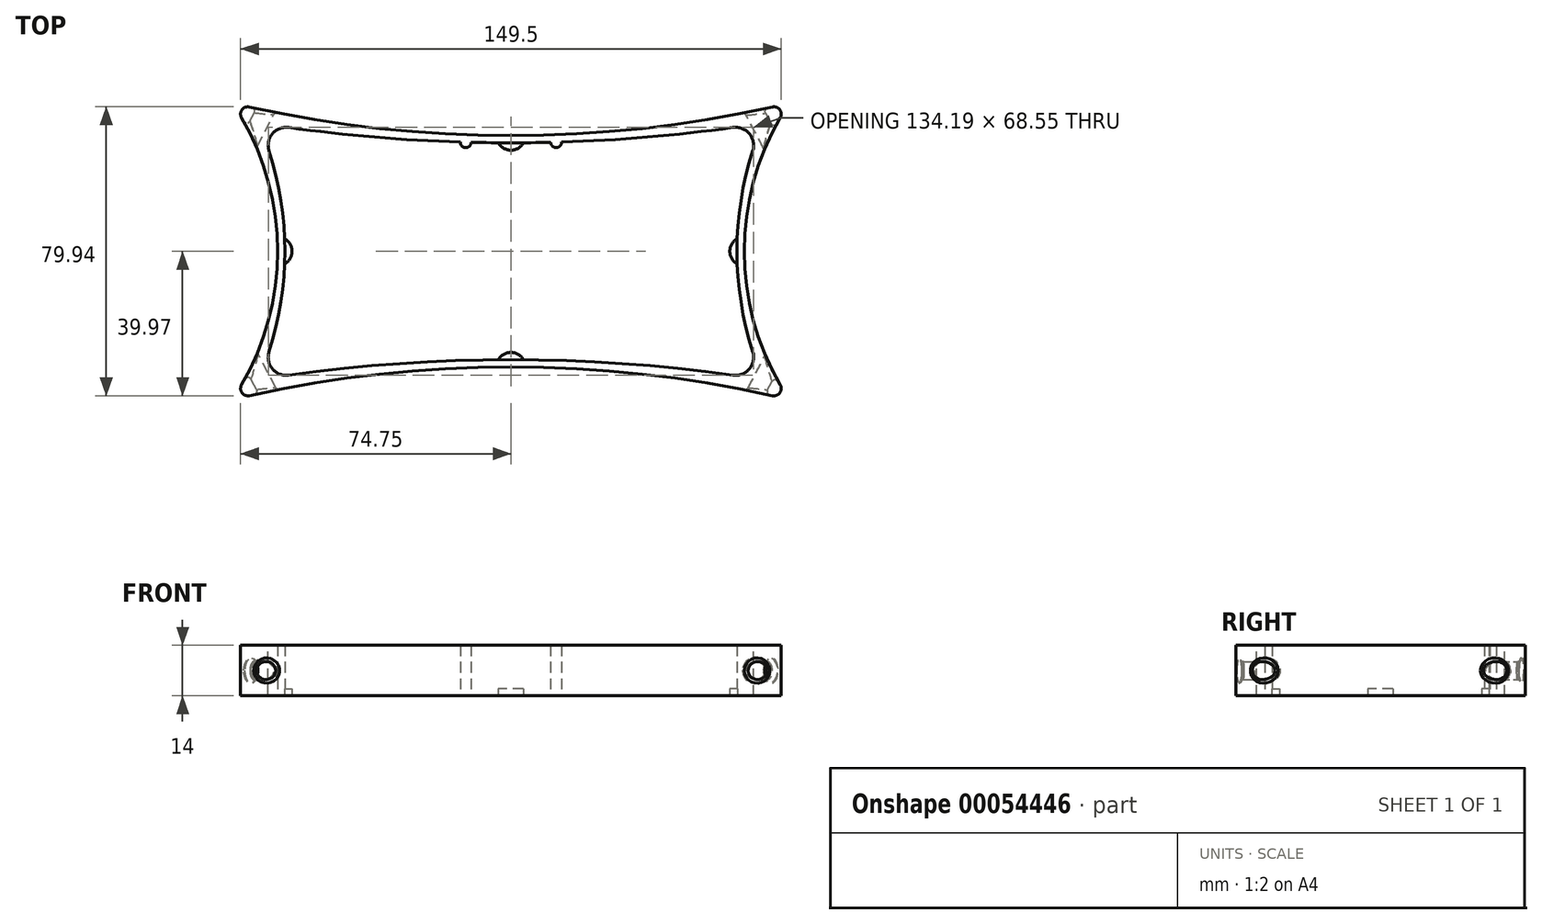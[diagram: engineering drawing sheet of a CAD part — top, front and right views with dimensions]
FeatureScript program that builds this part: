
annotation { "Feature Type Name" : "Feature", "Feature Type Description" : "" }
export const myFeature = defineFeature(function(context is Context, id is Id, definition is map)
    precondition{}
    {
        {
            var Q0;
            Q0=qCreatedBy(makeId("Top.planeOp"),FACE);
            var sketch = newSketch(context, id + "F0", { "sketchPlane" : qUnion([Q0])});
            skLineSegment(sketch, "E0.rect.bottom", {"start": v(77, -41) * mm, "end": v(-77, -41) * mm, "construction": true});
            skLineSegment(sketch, "E0.rect.top", {"start": v(77, 41) * mm, "end": v(-77, 41) * mm, "construction": true});
            skLineSegment(sketch, "E0.rect.left", {"start": v(77, -41) * mm, "end": v(77, 41) * mm, "construction": true});
            skLineSegment(sketch, "E0.rect.right", {"start": v(-77, -41) * mm, "end": v(-77, 41) * mm, "construction": true});
            skPoint(sketch, "E0.rect.middle", {"position": v(0, 0) * mm});
            skPoint(sketch, "E1.endSnap0", {"position": v(-77, 0) * mm});
            skPoint(sketch, "E2.endSnap0", {"position": v(0, 41) * mm});
            skLineSegment(sketch, "E3.rect.bottom", {"start": v(-62.5, 30) * mm, "end": v(62.5, 30) * mm, "construction": true});
            skLineSegment(sketch, "E3.rect.top", {"start": v(-62.5, -30) * mm, "end": v(62.5, -30) * mm, "construction": true});
            skLineSegment(sketch, "E3.rect.left", {"start": v(-62.5, 30) * mm, "end": v(-62.5, -30) * mm, "construction": true});
            skLineSegment(sketch, "E3.rect.right", {"start": v(62.5, 30) * mm, "end": v(62.5, -30) * mm, "construction": true});
            skArc(sketch, "E4", {"start": v(-77, -41) * mm, "mid": v(-64.5, 0) * mm, "end": v(-77, 41) * mm});
            skLineSegment(sketch, "E5", {"start": v(-77, 41) * mm, "end": v(-62.5, 30) * mm, "construction": true});
            skPoint(sketch, "E6.startSnap0", {"position": v(-69.75, 35.5) * mm});
            skLineSegment(sketch, "E7.MirrorCS", {"start": v(-77, -41) * mm, "end": v(-62.5, -30) * mm, "construction": true});
            skArc(sketch, "E8", {"start": v(-69.75, -35.5) * mm, "mid": v(-62.5, 0) * mm, "end": v(-69.75, 35.5) * mm});
            skLineSegment(sketch, "E9", {"start": v(-62.5, 0) * mm, "end": v(-64.5, 0) * mm, "construction": true});
            skArc(sketch, "E10", {"start": v(-77, 41) * mm, "mid": v(0, 32) * mm, "end": v(77, 41) * mm});
            skLineSegment(sketch, "E11", {"start": v(0, 30) * mm, "end": v(0, 32) * mm, "construction": true});
            skArc(sketch, "E12.MirrorCS", {"start": v(69.75, -35.5) * mm, "mid": v(62.5, 0) * mm, "end": v(69.75, 35.5) * mm});
            skArc(sketch, "E13.MirrorCS", {"start": v(77, -41) * mm, "mid": v(64.5, 0) * mm, "end": v(77, 41) * mm});
            skArc(sketch, "E14.MirrorCS", {"start": v(-77, -41) * mm, "mid": v(0, -32) * mm, "end": v(77, -41) * mm});
            skArc(sketch, "E15", {"start": v(-69.75, 35.5) * mm, "mid": v(0, 30) * mm, "end": v(69.75, 35.5) * mm});
            skArc(sketch, "E16.MirrorCS", {"start": v(-69.75, -35.5) * mm, "mid": v(0, -30) * mm, "end": v(69.75, -35.5) * mm});
            skLineSegment(sketch, "E17", {"start": v(0, 41) * mm, "end": v(0, 32) * mm, "construction": true});
            skLineSegment(sketch, "E18", {"start": v(-77, 0) * mm, "end": v(-64.5, 0) * mm, "construction": true});
            skLineSegment(sketch, "E19.bottom", {"start": v(-12.5, 30.18) * mm, "end": v(12.5, 30.18) * mm, "construction": true});
            skLineSegment(sketch, "E19.top", {"start": v(-12.5, -30.18) * mm, "end": v(12.5, -30.18) * mm, "construction": true});
            skLineSegment(sketch, "E19.left", {"start": v(-12.5, 30.18) * mm, "end": v(-12.5, -30.18) * mm, "construction": true});
            skLineSegment(sketch, "E19.right", {"start": v(12.5, 30.18) * mm, "end": v(12.5, -30.18) * mm, "construction": true});
            skLineSegment(sketch, "E20", {"start": v(-12.5, 0) * mm, "end": v(12.5, 0) * mm, "construction": true});
            skArc(sketch, "E21", {"start": v(-14, 30.22) * mm, "mid": v(-12.52, 28.68) * mm, "end": v(-11, 30.18) * mm});
            skArc(sketch, "E22.MirrorCS", {"start": v(14, 30.22) * mm, "mid": v(12.52, 28.68) * mm, "end": v(11, 30.18) * mm});
            skArc(sketch, "E23.MirrorCS", {"start": v(-14, -30.22) * mm, "mid": v(-12.52, -28.68) * mm, "end": v(-11, -30.18) * mm});
            skArc(sketch, "E24.MirrorCS", {"start": v(14, -30.22) * mm, "mid": v(12.52, -28.68) * mm, "end": v(11, -30.18) * mm});
            skSolve(sketch);
        }
        {
            var Q0;
            Q0 = qSketchRegion(id + "F0", true);
            var Q1;
            {var subQ0=sQuery(id+"F0.wireOp",EDGE,"E21");var subQ1=sQuery(id+"F0.wireOp",EDGE,"E15");var subQ2=makeQuery(id+"F0.imprint","INTERSECT",VERTEX,{"disambiguationData":[OD(0.0)],"derivedFrom":[subQ1,subQ0]});Q1=makeQuery(id+"F0.imprint","IMPRINT",FACE,{"disambiguationData":[TD([[makeQuery(id+"F0.imprint","IMPRINT",EDGE,{"disambiguationData":[TD([[subQ2,-1.0]])],"derivedFrom":subQ1}),-1.0]])]});}
            var Q2;
            {var subQ0=sQuery(id+"F0.wireOp",EDGE,"E22.MirrorCS");var subQ1=sQuery(id+"F0.wireOp",EDGE,"E15");var subQ2=makeQuery(id+"F0.imprint","INTERSECT",VERTEX,{"disambiguationData":[OD(0.0)],"derivedFrom":[subQ1,subQ0]});Q2=makeQuery(id+"F0.imprint","IMPRINT",FACE,{"disambiguationData":[TD([[makeQuery(id+"F0.imprint","IMPRINT",EDGE,{"disambiguationData":[TD([[subQ2,1.0]])],"derivedFrom":subQ1}),-1.0]])]});}
            var Q3;
            {var subQ0=sQuery(id+"F0.wireOp",EDGE,"E23.MirrorCS");var subQ1=sQuery(id+"F0.wireOp",EDGE,"E16.MirrorCS");var subQ2=makeQuery(id+"F0.imprint","INTERSECT",VERTEX,{"disambiguationData":[OD(0.0)],"derivedFrom":[subQ1,subQ0]});Q3=makeQuery(id+"F0.imprint","IMPRINT",FACE,{"disambiguationData":[TD([[makeQuery(id+"F0.imprint","IMPRINT",EDGE,{"disambiguationData":[TD([[subQ2,-1.0]])],"derivedFrom":subQ1}),1.0]])]});}
            var Q4;
            {var subQ0=sQuery(id+"F0.wireOp",EDGE,"E24.MirrorCS");var subQ1=sQuery(id+"F0.wireOp",EDGE,"E16.MirrorCS");var subQ2=makeQuery(id+"F0.imprint","INTERSECT",VERTEX,{"disambiguationData":[OD(0.0)],"derivedFrom":[subQ1,subQ0]});Q4=makeQuery(id+"F0.imprint","IMPRINT",FACE,{"disambiguationData":[TD([[makeQuery(id+"F0.imprint","IMPRINT",EDGE,{"disambiguationData":[TD([[subQ2,1.0]])],"derivedFrom":subQ1}),1.0]])]});}
            extrude(context, id + "F1", {"entities" : qUnion([Q0, Q1, Q2, Q3, Q4]), "depth" : 14 * mm});
        }
        {
            var Q0;
            Q0=makeQuery(id+"F1.opExtrude","SWEPT_EDGE",EDGE,{"disambiguationData":[OSD([sQuery(id+"F0.wireOp",EDGE,"ea470add-b846-47a1-99bc-41ed1cdb80660.MirrorCS"),sQuery(id+"F0.wireOp",EDGE,"4994bbe1-2ed1-413a-9b23-e4b9f51bf674")])]});
            var Q1;
            Q1=makeQuery(id+"F1.opExtrude","SWEPT_EDGE",EDGE,{"disambiguationData":[OSD([sQuery(id+"F0.wireOp",EDGE,"E8"),sQuery(id+"F0.wireOp",EDGE,"4994bbe1-2ed1-413a-9b23-e4b9f51bf674")])]});
            var Q2;
            Q2=makeQuery(id+"F1.opExtrude","SWEPT_EDGE",EDGE,{"disambiguationData":[OSD([sQuery(id+"F0.wireOp",EDGE,"E8"),sQuery(id+"F0.wireOp",EDGE,"cdb18601-847e-4306-8674-6f4c30cc67390.MirrorCS")])]});
            var Q3;
            Q3=makeQuery(id+"F1.opExtrude","SWEPT_EDGE",EDGE,{"disambiguationData":[OSD([sQuery(id+"F0.wireOp",EDGE,"ea470add-b846-47a1-99bc-41ed1cdb80660.MirrorCS"),sQuery(id+"F0.wireOp",EDGE,"cdb18601-847e-4306-8674-6f4c30cc67390.MirrorCS")])]});
            var Q4;
            Q4=makeQuery(id+"F1.opExtrude","SWEPT_EDGE",EDGE,{"disambiguationData":[OSD([sQuery(id+"F0.wireOp",EDGE,"E12.MirrorCS"),sQuery(id+"F0.wireOp",EDGE,"E16.MirrorCS")])]});
            var Q5;
            Q5=makeQuery(id+"F1.opExtrude","SWEPT_EDGE",EDGE,{"disambiguationData":[OSD([sQuery(id+"F0.wireOp",EDGE,"E12.MirrorCS"),sQuery(id+"F0.wireOp",EDGE,"E15")])]});
            fillet(context, id + "F2", {"entities" : qUnion([Q0, Q1, Q2, Q3, Q4, Q5]), "radius" : 5 * mm, "tangentPropagation" : true, "allowEdgeOverflow" : false});
        }
        {
            var Q0;
            Q0=makeQuery(id+"F1.opExtrude","SWEPT_EDGE",EDGE,{"disambiguationData":[OSD([sQuery(id+"F0.wireOp",EDGE,"E4"),sQuery(id+"F0.wireOp",EDGE,"E14.MirrorCS")])]});
            var Q1;
            Q1=makeQuery(id+"F1.opExtrude","SWEPT_EDGE",EDGE,{"disambiguationData":[OSD([sQuery(id+"F0.wireOp",EDGE,"E13.MirrorCS"),sQuery(id+"F0.wireOp",EDGE,"E14.MirrorCS")])]});
            var Q2;
            Q2=makeQuery(id+"F1.opExtrude","SWEPT_EDGE",EDGE,{"disambiguationData":[OSD([sQuery(id+"F0.wireOp",EDGE,"E10"),sQuery(id+"F0.wireOp",EDGE,"E13.MirrorCS")])]});
            var Q3;
            Q3=makeQuery(id+"F1.opExtrude","SWEPT_EDGE",EDGE,{"disambiguationData":[OSD([sQuery(id+"F0.wireOp",EDGE,"E4"),sQuery(id+"F0.wireOp",EDGE,"E10")])]});
            fillet(context, id + "F3", {"entities" : qUnion([Q0, Q1, Q2, Q3]), "radius" : 2 * mm, "tangentPropagation" : true, "allowEdgeOverflow" : false});
        }
        {
            var Q0;
            {var subQ0=sQuery(id+"F0.wireOp",EDGE,"E14.MirrorCS");var subQ1=sQuery(id+"F0.wireOp",EDGE,"E4");Q0=makeQuery(id+"F3.opFillet","BLEND_VERTEX",VERTEX,{"blendedFrom":[makeQuery(id+"F1.opExtrude","SWEPT_EDGE",EDGE,{"disambiguationData":[OSD([subQ1,subQ0])]}),makeQuery(id+"F1.opExtrude","SWEPT_FACE",FACE,{"disambiguationData":[OSD([subQ0])]}),makeQuery(id+"F1.opExtrude","CAP_FACE",FACE,{"disambiguationData":[OSD([subQ1,sQuery(id+"F0.wireOp",EDGE,"E8"),sQuery(id+"F0.wireOp",EDGE,"E10"),sQuery(id+"F0.wireOp",EDGE,"E12.MirrorCS"),sQuery(id+"F0.wireOp",EDGE,"E13.MirrorCS"),subQ0,sQuery(id+"F0.wireOp",EDGE,"E15"),sQuery(id+"F0.wireOp",EDGE,"E16.MirrorCS"),sQuery(id+"F0.wireOp",EDGE,"E21"),sQuery(id+"F0.wireOp",EDGE,"E22.MirrorCS"),sQuery(id+"F0.wireOp",EDGE,"E23.MirrorCS"),sQuery(id+"F0.wireOp",EDGE,"E24.MirrorCS")])],"isStart":false})],"blendedInto":[makeQuery(id+"F1.opExtrude","SWEPT_FACE",FACE,{"disambiguationData":[OSD([subQ0])]}),makeQuery(id+"F1.opExtrude","CAP_FACE",FACE,{"disambiguationData":[OSD([subQ1,sQuery(id+"F0.wireOp",EDGE,"E8"),sQuery(id+"F0.wireOp",EDGE,"E10"),sQuery(id+"F0.wireOp",EDGE,"E12.MirrorCS"),sQuery(id+"F0.wireOp",EDGE,"E13.MirrorCS"),subQ0,sQuery(id+"F0.wireOp",EDGE,"E15"),sQuery(id+"F0.wireOp",EDGE,"E16.MirrorCS"),sQuery(id+"F0.wireOp",EDGE,"E21"),sQuery(id+"F0.wireOp",EDGE,"E22.MirrorCS"),sQuery(id+"F0.wireOp",EDGE,"E23.MirrorCS"),sQuery(id+"F0.wireOp",EDGE,"E24.MirrorCS")])],"isStart":false})]});}
            var Q1;
            {var subQ0=sQuery(id+"F0.wireOp",EDGE,"E14.MirrorCS");var subQ1=sQuery(id+"F0.wireOp",EDGE,"E4");Q1=makeQuery(id+"F3.opFillet","BLEND_VERTEX",VERTEX,{"blendedFrom":[makeQuery(id+"F1.opExtrude","SWEPT_EDGE",EDGE,{"disambiguationData":[OSD([subQ1,subQ0])]}),makeQuery(id+"F1.opExtrude","SWEPT_FACE",FACE,{"disambiguationData":[OSD([subQ0])]}),makeQuery(id+"F1.opExtrude","CAP_FACE",FACE,{"disambiguationData":[OSD([subQ1,sQuery(id+"F0.wireOp",EDGE,"E8"),sQuery(id+"F0.wireOp",EDGE,"E10"),sQuery(id+"F0.wireOp",EDGE,"E12.MirrorCS"),sQuery(id+"F0.wireOp",EDGE,"E13.MirrorCS"),subQ0,sQuery(id+"F0.wireOp",EDGE,"E15"),sQuery(id+"F0.wireOp",EDGE,"E16.MirrorCS"),sQuery(id+"F0.wireOp",EDGE,"E21"),sQuery(id+"F0.wireOp",EDGE,"E22.MirrorCS"),sQuery(id+"F0.wireOp",EDGE,"E23.MirrorCS"),sQuery(id+"F0.wireOp",EDGE,"E24.MirrorCS")])],"isStart":true})],"blendedInto":[makeQuery(id+"F1.opExtrude","SWEPT_FACE",FACE,{"disambiguationData":[OSD([subQ0])]}),makeQuery(id+"F1.opExtrude","CAP_FACE",FACE,{"disambiguationData":[OSD([subQ1,sQuery(id+"F0.wireOp",EDGE,"E8"),sQuery(id+"F0.wireOp",EDGE,"E10"),sQuery(id+"F0.wireOp",EDGE,"E12.MirrorCS"),sQuery(id+"F0.wireOp",EDGE,"E13.MirrorCS"),subQ0,sQuery(id+"F0.wireOp",EDGE,"E15"),sQuery(id+"F0.wireOp",EDGE,"E16.MirrorCS"),sQuery(id+"F0.wireOp",EDGE,"E21"),sQuery(id+"F0.wireOp",EDGE,"E22.MirrorCS"),sQuery(id+"F0.wireOp",EDGE,"E23.MirrorCS"),sQuery(id+"F0.wireOp",EDGE,"E24.MirrorCS")])],"isStart":true})]});}
            var Q2;
            {var subQ0=sQuery(id+"F0.wireOp",EDGE,"E13.MirrorCS");var subQ1=sQuery(id+"F0.wireOp",EDGE,"E10");Q2=makeQuery(id+"F3.opFillet","BLEND_VERTEX",VERTEX,{"blendedFrom":[makeQuery(id+"F1.opExtrude","SWEPT_EDGE",EDGE,{"disambiguationData":[OSD([subQ1,subQ0])]}),makeQuery(id+"F1.opExtrude","SWEPT_FACE",FACE,{"disambiguationData":[OSD([subQ0])]}),makeQuery(id+"F1.opExtrude","CAP_FACE",FACE,{"disambiguationData":[OSD([sQuery(id+"F0.wireOp",EDGE,"E4"),sQuery(id+"F0.wireOp",EDGE,"E8"),subQ1,sQuery(id+"F0.wireOp",EDGE,"E12.MirrorCS"),subQ0,sQuery(id+"F0.wireOp",EDGE,"E14.MirrorCS"),sQuery(id+"F0.wireOp",EDGE,"E15"),sQuery(id+"F0.wireOp",EDGE,"E16.MirrorCS"),sQuery(id+"F0.wireOp",EDGE,"E21"),sQuery(id+"F0.wireOp",EDGE,"E22.MirrorCS"),sQuery(id+"F0.wireOp",EDGE,"E23.MirrorCS"),sQuery(id+"F0.wireOp",EDGE,"E24.MirrorCS")])],"isStart":false})],"blendedInto":[makeQuery(id+"F1.opExtrude","SWEPT_FACE",FACE,{"disambiguationData":[OSD([subQ0])]}),makeQuery(id+"F1.opExtrude","CAP_FACE",FACE,{"disambiguationData":[OSD([sQuery(id+"F0.wireOp",EDGE,"E4"),sQuery(id+"F0.wireOp",EDGE,"E8"),subQ1,sQuery(id+"F0.wireOp",EDGE,"E12.MirrorCS"),subQ0,sQuery(id+"F0.wireOp",EDGE,"E14.MirrorCS"),sQuery(id+"F0.wireOp",EDGE,"E15"),sQuery(id+"F0.wireOp",EDGE,"E16.MirrorCS"),sQuery(id+"F0.wireOp",EDGE,"E21"),sQuery(id+"F0.wireOp",EDGE,"E22.MirrorCS"),sQuery(id+"F0.wireOp",EDGE,"E23.MirrorCS"),sQuery(id+"F0.wireOp",EDGE,"E24.MirrorCS")])],"isStart":false})]});}
            cPlane(context, id + "F4", {"entities" : qUnion([Q0, Q1, Q2]), "cplaneType" : CPlaneType.THREE_POINT, "offset" : 25 * mm, "width" : 150 * mm, "height" : 150 * mm});
        }
        {
            var Q0;
            Q0=qCreatedBy(id+"F4.planeOp",FACE);
            var sketch = newSketch(context, id + "F5", { "sketchPlane" : qUnion([Q0])});
            skLineSegment(sketch, "E25.0", {"start": v(82.58, 14) * mm, "end": v(82.58, 0) * mm, "construction": true});
            skLineSegment(sketch, "E26", {"start": v(82.58, 7) * mm, "end": v(77.58, 7) * mm, "construction": true});
            skLineSegment(sketch, "E27", {"start": v(0, 1.7) * mm, "end": v(0, 15.7) * mm, "construction": true});
            skCircle(sketch, "E28", {"center": v(77.58, 7) * mm, "radius": 2.5 * mm});
            skCircle(sketch, "E29.MirrorC", {"center": v(-77.58, 7) * mm, "radius": 2.5 * mm});
            skSolve(sketch);
        }
        {
            var Q0;
            Q0 = qSketchRegion(id + "F5", true);
            extrude(context, id + "F6", {"entities" : qUnion([Q0]), "operationType" : NewBodyOperationType.REMOVE, "endBound" : BoundingType.THROUGH_ALL, "oppositeDirection" : true, "depth" : 25 * mm, "hasSecondDirection" : true, "secondDirectionBound" : SecondDirectionBoundingType.THROUGH_ALL, "secondDirectionOppositeDirection" : false, "secondDirectionDepth" : 25 * mm});
        }
        {
            var Q0;
            {var subQ0=sQuery(id+"F0.wireOp",EDGE,"E10");var subQ1=sQuery(id+"F0.wireOp",EDGE,"E4");Q0=makeQuery(id+"F3.opFillet","BLEND_VERTEX",VERTEX,{"blendedFrom":[makeQuery(id+"F1.opExtrude","SWEPT_EDGE",EDGE,{"disambiguationData":[OSD([subQ1,subQ0])]}),makeQuery(id+"F1.opExtrude","SWEPT_FACE",FACE,{"disambiguationData":[OSD([subQ1])]}),makeQuery(id+"F1.opExtrude","CAP_FACE",FACE,{"disambiguationData":[OSD([subQ1,sQuery(id+"F0.wireOp",EDGE,"E8"),subQ0,sQuery(id+"F0.wireOp",EDGE,"E12.MirrorCS"),sQuery(id+"F0.wireOp",EDGE,"E13.MirrorCS"),sQuery(id+"F0.wireOp",EDGE,"E14.MirrorCS"),sQuery(id+"F0.wireOp",EDGE,"E15"),sQuery(id+"F0.wireOp",EDGE,"E16.MirrorCS"),sQuery(id+"F0.wireOp",EDGE,"E21"),sQuery(id+"F0.wireOp",EDGE,"E22.MirrorCS"),sQuery(id+"F0.wireOp",EDGE,"E23.MirrorCS"),sQuery(id+"F0.wireOp",EDGE,"E24.MirrorCS")])],"isStart":false})],"blendedInto":[makeQuery(id+"F1.opExtrude","SWEPT_FACE",FACE,{"disambiguationData":[OSD([subQ1])]}),makeQuery(id+"F1.opExtrude","CAP_FACE",FACE,{"disambiguationData":[OSD([subQ1,sQuery(id+"F0.wireOp",EDGE,"E8"),subQ0,sQuery(id+"F0.wireOp",EDGE,"E12.MirrorCS"),sQuery(id+"F0.wireOp",EDGE,"E13.MirrorCS"),sQuery(id+"F0.wireOp",EDGE,"E14.MirrorCS"),sQuery(id+"F0.wireOp",EDGE,"E15"),sQuery(id+"F0.wireOp",EDGE,"E16.MirrorCS"),sQuery(id+"F0.wireOp",EDGE,"E21"),sQuery(id+"F0.wireOp",EDGE,"E22.MirrorCS"),sQuery(id+"F0.wireOp",EDGE,"E23.MirrorCS"),sQuery(id+"F0.wireOp",EDGE,"E24.MirrorCS")])],"isStart":false})]});}
            var Q1;
            {var subQ0=sQuery(id+"F0.wireOp",EDGE,"E10");var subQ1=sQuery(id+"F0.wireOp",EDGE,"E4");Q1=makeQuery(id+"F3.opFillet","BLEND_VERTEX",VERTEX,{"blendedFrom":[makeQuery(id+"F1.opExtrude","SWEPT_EDGE",EDGE,{"disambiguationData":[OSD([subQ1,subQ0])]}),makeQuery(id+"F1.opExtrude","SWEPT_FACE",FACE,{"disambiguationData":[OSD([subQ1])]}),makeQuery(id+"F1.opExtrude","CAP_FACE",FACE,{"disambiguationData":[OSD([subQ1,sQuery(id+"F0.wireOp",EDGE,"E8"),subQ0,sQuery(id+"F0.wireOp",EDGE,"E12.MirrorCS"),sQuery(id+"F0.wireOp",EDGE,"E13.MirrorCS"),sQuery(id+"F0.wireOp",EDGE,"E14.MirrorCS"),sQuery(id+"F0.wireOp",EDGE,"E15"),sQuery(id+"F0.wireOp",EDGE,"E16.MirrorCS"),sQuery(id+"F0.wireOp",EDGE,"E21"),sQuery(id+"F0.wireOp",EDGE,"E22.MirrorCS"),sQuery(id+"F0.wireOp",EDGE,"E23.MirrorCS"),sQuery(id+"F0.wireOp",EDGE,"E24.MirrorCS")])],"isStart":true})],"blendedInto":[makeQuery(id+"F1.opExtrude","SWEPT_FACE",FACE,{"disambiguationData":[OSD([subQ1])]}),makeQuery(id+"F1.opExtrude","CAP_FACE",FACE,{"disambiguationData":[OSD([subQ1,sQuery(id+"F0.wireOp",EDGE,"E8"),subQ0,sQuery(id+"F0.wireOp",EDGE,"E12.MirrorCS"),sQuery(id+"F0.wireOp",EDGE,"E13.MirrorCS"),sQuery(id+"F0.wireOp",EDGE,"E14.MirrorCS"),sQuery(id+"F0.wireOp",EDGE,"E15"),sQuery(id+"F0.wireOp",EDGE,"E16.MirrorCS"),sQuery(id+"F0.wireOp",EDGE,"E21"),sQuery(id+"F0.wireOp",EDGE,"E22.MirrorCS"),sQuery(id+"F0.wireOp",EDGE,"E23.MirrorCS"),sQuery(id+"F0.wireOp",EDGE,"E24.MirrorCS")])],"isStart":true})]});}
            var Q2;
            {var subQ0=sQuery(id+"F0.wireOp",EDGE,"E14.MirrorCS");var subQ1=sQuery(id+"F0.wireOp",EDGE,"E13.MirrorCS");Q2=makeQuery(id+"F3.opFillet","BLEND_VERTEX",VERTEX,{"blendedFrom":[makeQuery(id+"F1.opExtrude","SWEPT_EDGE",EDGE,{"disambiguationData":[OSD([subQ1,subQ0])]}),makeQuery(id+"F1.opExtrude","SWEPT_FACE",FACE,{"disambiguationData":[OSD([subQ0])]}),makeQuery(id+"F1.opExtrude","CAP_FACE",FACE,{"disambiguationData":[OSD([sQuery(id+"F0.wireOp",EDGE,"E4"),sQuery(id+"F0.wireOp",EDGE,"E8"),sQuery(id+"F0.wireOp",EDGE,"E10"),sQuery(id+"F0.wireOp",EDGE,"E12.MirrorCS"),subQ1,subQ0,sQuery(id+"F0.wireOp",EDGE,"E15"),sQuery(id+"F0.wireOp",EDGE,"E16.MirrorCS"),sQuery(id+"F0.wireOp",EDGE,"E21"),sQuery(id+"F0.wireOp",EDGE,"E22.MirrorCS"),sQuery(id+"F0.wireOp",EDGE,"E23.MirrorCS"),sQuery(id+"F0.wireOp",EDGE,"E24.MirrorCS")])],"isStart":false})],"blendedInto":[makeQuery(id+"F1.opExtrude","SWEPT_FACE",FACE,{"disambiguationData":[OSD([subQ0])]}),makeQuery(id+"F1.opExtrude","CAP_FACE",FACE,{"disambiguationData":[OSD([sQuery(id+"F0.wireOp",EDGE,"E4"),sQuery(id+"F0.wireOp",EDGE,"E8"),sQuery(id+"F0.wireOp",EDGE,"E10"),sQuery(id+"F0.wireOp",EDGE,"E12.MirrorCS"),subQ1,subQ0,sQuery(id+"F0.wireOp",EDGE,"E15"),sQuery(id+"F0.wireOp",EDGE,"E16.MirrorCS"),sQuery(id+"F0.wireOp",EDGE,"E21"),sQuery(id+"F0.wireOp",EDGE,"E22.MirrorCS"),sQuery(id+"F0.wireOp",EDGE,"E23.MirrorCS"),sQuery(id+"F0.wireOp",EDGE,"E24.MirrorCS")])],"isStart":false})]});}
            cPlane(context, id + "F7", {"entities" : qUnion([Q0, Q1, Q2]), "cplaneType" : CPlaneType.THREE_POINT, "offset" : 25 * mm, "width" : 150 * mm, "height" : 150 * mm});
        }
        {
            var Q0;
            Q0=qCreatedBy(id+"F7.planeOp",FACE);
            var sketch = newSketch(context, id + "F8", { "sketchPlane" : qUnion([Q0])});
            skLineSegment(sketch, "E30.0", {"start": v(83.12, 14) * mm, "end": v(83.12, 0) * mm, "construction": true});
            skLineSegment(sketch, "E31", {"start": v(0, 0) * mm, "end": v(0, 14) * mm, "construction": true});
            skLineSegment(sketch, "E32", {"start": v(83.12, 7) * mm, "end": v(78.12, 7) * mm, "construction": true});
            skCircle(sketch, "E33", {"center": v(78.12, 7) * mm, "radius": 2.5 * mm});
            skCircle(sketch, "E34.MirrorC", {"center": v(-78.12, 7) * mm, "radius": 2.5 * mm});
            skSolve(sketch);
        }
        {
            var Q0;
            Q0 = qSketchRegion(id + "F8", true);
            extrude(context, id + "F9", {"entities" : qUnion([Q0]), "operationType" : NewBodyOperationType.REMOVE, "endBound" : BoundingType.THROUGH_ALL, "oppositeDirection" : true, "depth" : 25 * mm, "hasSecondDirection" : true, "secondDirectionBound" : SecondDirectionBoundingType.THROUGH_ALL, "secondDirectionOppositeDirection" : false, "secondDirectionDepth" : 25 * mm});
        }
        {
            var Q0;
            Q0=qCreatedBy(makeId("Top.planeOp"),FACE);
            var sketch = newSketch(context, id + "F10", { "sketchPlane" : qUnion([Q0])});
            skArc(sketch, "E35.0", {"start": v(-11, 30.14) * mm, "mid": v(0, 30) * mm, "end": v(11, 30.14) * mm});
            skArc(sketch, "E36.0", {"start": v(-66.86, -27.77) * mm, "mid": v(-62.5, 0) * mm, "end": v(-66.86, 27.77) * mm});
            skArc(sketch, "E37.0", {"start": v(66.86, -27.77) * mm, "mid": v(62.5, 0) * mm, "end": v(66.86, 27.77) * mm});
            skArc(sketch, "E38.0", {"start": v(-11, -30.14) * mm, "mid": v(0, -30) * mm, "end": v(11, -30.14) * mm});
            skArc(sketch, "E39", {"start": v(-3.5, 30.01) * mm, "mid": v(0, 27.98) * mm, "end": v(3.5, 30.01) * mm});
            skLineSegment(sketch, "E40", {"start": v(0, 30.01) * mm, "end": v(0, 0) * mm, "construction": true});
            skLineSegment(sketch, "E41", {"start": v(0, 0) * mm, "end": v(-62.57, 0) * mm, "construction": true});
            skArc(sketch, "E42", {"start": v(-62.57, -3.5) * mm, "mid": v(-60.5, 0) * mm, "end": v(-62.57, 3.5) * mm});
            skArc(sketch, "E43.0", {"start": v(-72.31, 39.92) * mm, "mid": v(0, 32) * mm, "end": v(72.31, 39.92) * mm, "construction": true});
            skArc(sketch, "E44.0", {"start": v(-74.47, -36.97) * mm, "mid": v(-64.5, 0) * mm, "end": v(-74.47, 36.97) * mm, "construction": true});
            skLineSegment(sketch, "E45", {"start": v(-62.57, 3.5) * mm, "end": v(-62.57, -3.5) * mm, "construction": true});
            skLineSegment(sketch, "E46", {"start": v(-3.5, 30.01) * mm, "end": v(3.5, 30.01) * mm, "construction": true});
            skPoint(sketch, "E47", {"position": v(0, 30.01) * mm});
            skArc(sketch, "E48.MirrorCS", {"start": v(62.57, -3.5) * mm, "mid": v(60.5, 0) * mm, "end": v(62.57, 3.5) * mm});
            skLineSegment(sketch, "E49.MirrorCS", {"start": v(62.57, 3.5) * mm, "end": v(62.57, -3.5) * mm, "construction": true});
            skArc(sketch, "E50.MirrorCS", {"start": v(-3.5, -30.01) * mm, "mid": v(0, -27.98) * mm, "end": v(3.5, -30.01) * mm});
            skLineSegment(sketch, "E51.MirrorCS", {"start": v(-3.5, -30.01) * mm, "end": v(3.5, -30.01) * mm, "construction": true});
            skSolve(sketch);
        }
        {
            var Q0;
            Q0 = qSketchRegion(id + "F10", true);
            extrude(context, id + "F11", {"entities" : qUnion([Q0]), "operationType" : NewBodyOperationType.ADD, "depth" : 2 * mm});
        }
        {
            var Q0;
            Q0=makeQuery(id+"F11.opExtrude","CAP_EDGE",EDGE,{"disambiguationData":[OSD([sQuery(id+"F10.wireOp",EDGE,"E36.0")])],"isStart":false});
            var Q1;
            Q1=makeQuery(id+"F11.opExtrude","CAP_EDGE",EDGE,{"disambiguationData":[OSD([sQuery(id+"F10.wireOp",EDGE,"E35.0")])],"isStart":false});
            var Q2;
            Q2=makeQuery(id+"F11.opExtrude","CAP_EDGE",EDGE,{"disambiguationData":[OSD([sQuery(id+"F10.wireOp",EDGE,"E37.0")])],"isStart":false});
            var Q3;
            Q3=makeQuery(id+"F11.opExtrude","CAP_EDGE",EDGE,{"disambiguationData":[OSD([sQuery(id+"F10.wireOp",EDGE,"E38.0")])],"isStart":false});
            var Q4;
            Q4=makeQuery(id+"F9.boolean.opBoolean","INTERSECT",EDGE,{"derivedFrom":[makeQuery(id+"F1.opExtrude","SWEPT_FACE",FACE,{"disambiguationData":[OSD([sQuery(id+"F0.wireOp",EDGE,"E10")])]}),makeQuery(id+"F9.opExtrude","SWEPT_FACE",FACE,{"disambiguationData":[OSD([sQuery(id+"F8.wireOp",EDGE,"E33")])]})]});
            var Q5;
            Q5=makeQuery(id+"F9.boolean.opBoolean","INTERSECT",EDGE,{"derivedFrom":[makeQuery(id+"F1.opExtrude","SWEPT_FACE",FACE,{"disambiguationData":[OSD([sQuery(id+"F0.wireOp",EDGE,"E4")])]}),makeQuery(id+"F9.opExtrude","SWEPT_FACE",FACE,{"disambiguationData":[OSD([sQuery(id+"F8.wireOp",EDGE,"E33")])]})]});
            var Q6;
            Q6=makeQuery(id+"F6.boolean.opBoolean","INTERSECT",EDGE,{"derivedFrom":[makeQuery(id+"F1.opExtrude","SWEPT_FACE",FACE,{"disambiguationData":[OSD([sQuery(id+"F0.wireOp",EDGE,"E4")])]}),makeQuery(id+"F6.opExtrude","SWEPT_FACE",FACE,{"disambiguationData":[OSD([sQuery(id+"F5.wireOp",EDGE,"E28")])]})]});
            var Q7;
            Q7=makeQuery(id+"F6.boolean.opBoolean","INTERSECT",EDGE,{"derivedFrom":[makeQuery(id+"F1.opExtrude","SWEPT_FACE",FACE,{"disambiguationData":[OSD([sQuery(id+"F0.wireOp",EDGE,"E14.MirrorCS")])]}),makeQuery(id+"F6.opExtrude","SWEPT_FACE",FACE,{"disambiguationData":[OSD([sQuery(id+"F5.wireOp",EDGE,"E28")])]})]});
            var Q8;
            Q8=makeQuery(id+"F9.boolean.opBoolean","INTERSECT",EDGE,{"derivedFrom":[makeQuery(id+"F1.opExtrude","SWEPT_FACE",FACE,{"disambiguationData":[OSD([sQuery(id+"F0.wireOp",EDGE,"E14.MirrorCS")])]}),makeQuery(id+"F9.opExtrude","SWEPT_FACE",FACE,{"disambiguationData":[OSD([sQuery(id+"F8.wireOp",EDGE,"E34.MirrorC")])]})]});
            var Q9;
            Q9=makeQuery(id+"F9.boolean.opBoolean","INTERSECT",EDGE,{"derivedFrom":[makeQuery(id+"F1.opExtrude","SWEPT_FACE",FACE,{"disambiguationData":[OSD([sQuery(id+"F0.wireOp",EDGE,"E13.MirrorCS")])]}),makeQuery(id+"F9.opExtrude","SWEPT_FACE",FACE,{"disambiguationData":[OSD([sQuery(id+"F8.wireOp",EDGE,"E34.MirrorC")])]})]});
            var Q10;
            Q10=makeQuery(id+"F6.boolean.opBoolean","INTERSECT",EDGE,{"derivedFrom":[makeQuery(id+"F1.opExtrude","SWEPT_FACE",FACE,{"disambiguationData":[OSD([sQuery(id+"F0.wireOp",EDGE,"E13.MirrorCS")])]}),makeQuery(id+"F6.opExtrude","SWEPT_FACE",FACE,{"disambiguationData":[OSD([sQuery(id+"F5.wireOp",EDGE,"E29.MirrorC")])]})]});
            var Q11;
            Q11=makeQuery(id+"F6.boolean.opBoolean","INTERSECT",EDGE,{"derivedFrom":[makeQuery(id+"F1.opExtrude","SWEPT_FACE",FACE,{"disambiguationData":[OSD([sQuery(id+"F0.wireOp",EDGE,"E10")])]}),makeQuery(id+"F6.opExtrude","SWEPT_FACE",FACE,{"disambiguationData":[OSD([sQuery(id+"F5.wireOp",EDGE,"E29.MirrorC")])]})]});
            fillet(context, id + "F12", {"entities" : qUnion([Q0, Q1, Q2, Q3, Q4, Q5, Q6, Q7, Q8, Q9, Q10, Q11]), "radius" : 1 * mm, "tangentPropagation" : true, "allowEdgeOverflow" : false});
        }
    });
